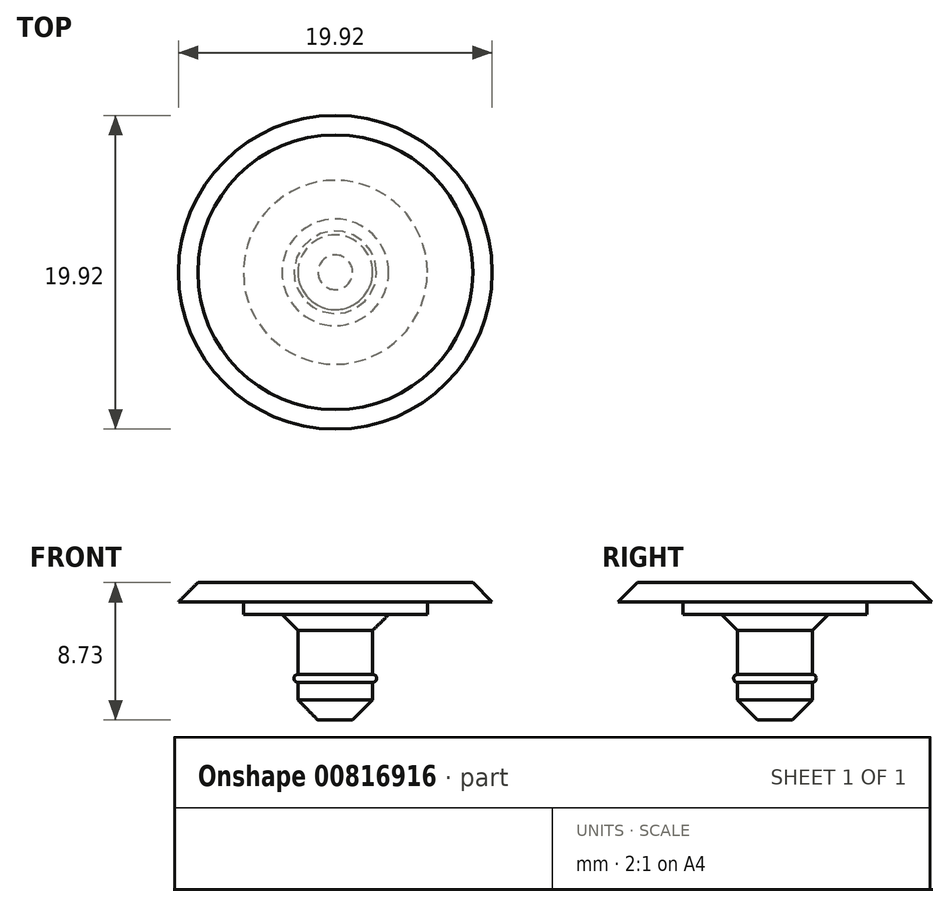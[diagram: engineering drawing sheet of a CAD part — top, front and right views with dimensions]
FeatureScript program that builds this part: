
annotation { "Feature Type Name" : "Feature", "Feature Type Description" : "" }
export const myFeature = defineFeature(function(context is Context, id is Id, definition is map)
    precondition{}
    {
        {
            var Q0;
            Q0=qCreatedBy(makeId("Front.planeOp"),FACE);
            var sketch = newSketch(context, id + "F0", { "sketchPlane" : qUnion([Q0])});
            skLineSegment(sketch, "E0", {"start": v(4.22, 0) * mm, "end": v(10, 0) * mm});
            skLineSegment(sketch, "E1", {"start": v(10, 0) * mm, "end": v(10, 2.03) * mm});
            skLineSegment(sketch, "E2", {"start": v(0, 2.03) * mm, "end": v(0, 0) * mm});
            skLineSegment(sketch, "E3", {"start": v(2.37, 0) * mm, "end": v(2.68, 0) * mm});
            skLineSegment(sketch, "E4", {"start": v(2.37, 0) * mm, "end": v(2.37, -3.8) * mm});
            skLineSegment(sketch, "E5", {"start": v(2.37, -6.7) * mm, "end": v(0, -6.7) * mm});
            skLineSegment(sketch, "E6", {"start": v(0, -6.7) * mm, "end": v(0, 0) * mm});
            skArc(sketch, "E7", {"start": v(2.37, -4.3) * mm, "mid": v(2.63, -4.05) * mm, "end": v(2.37, -3.8) * mm});
            skLineSegment(sketch, "E8.trimOffspring", {"start": v(2.37, -4.3) * mm, "end": v(2.37, -6.7) * mm});
            skLineSegment(sketch, "E9", {"start": v(2.68, 0) * mm, "end": v(4.22, 0) * mm});
            skLineSegment(sketch, "E10", {"start": v(0, 2.03) * mm, "end": v(10, 2.03) * mm});
            skPoint(sketch, "E11.center.orphan", {"position": v(0, 15.24) * mm});
            skSolve(sketch);
        }
        {
            var Q0;
            Q0=qSketchRegion(id+"F0",true);
            var Q1;
            Q1=sQuery(id+"F0.wireOp",EDGE,"E2");
            revolve(context, id + "F1", {"surfaceOperationType" : NewSurfaceOperationType.NEW, "entities" : qUnion([Q0]), "axis" : qUnion([Q1]), "revolveType" : RevolveType.FULL});
        }
        {
            var Q0;
            Q0=makeQuery(id+"F1.opRevolve","SWEPT_EDGE",EDGE,{"disambiguationData":[OSD([sQuery(id+"F0.wireOp",EDGE,"E5"),sQuery(id+"F0.wireOp",EDGE,"E8.trimOffspring")])]});
            chamfer(context, id + "F2", {"entities" : qUnion([Q0]), "width" : 1.27 * mm, "tangentPropagation" : true});
        }
        {
            var Q0;
            Q0=makeQuery(id+"F1.opRevolve","SWEPT_FACE",FACE,{"disambiguationData":[OSD([sQuery(id+"F0.wireOp",EDGE,"E0"),sQuery(id+"F0.wireOp",EDGE,"E3"),sQuery(id+"F0.wireOp",EDGE,"E9")])]});
            var sketch = newSketch(context, id + "F3", { "sketchPlane" : qUnion([Q0])});
            skCircle(sketch, "E12", {"center": v(0, 0) * mm, "radius": 5.84 * mm});
            skCircle(sketch, "E13", {"center": v(0, 0) * mm, "radius": 14.28 * mm});
            skSolve(sketch);
        }
        {
            var Q0;
            Q0=makeQuery(id+"F3.imprint","IMPRINT",FACE,{"disambiguationData":[TD([[makeQuery(id+"F3.imprint","IMPRINT",EDGE,{"derivedFrom":sQuery(id+"F3.wireOp",EDGE,"E13")}),1.0]])]});
            var Q1;
            Q1=makeQuery(id+"F3.imprint","IMPRINT",FACE,{"disambiguationData":[TD([[makeQuery(id+"F3.imprint","IMPRINT",EDGE,{"derivedFrom":sQuery(id+"F3.wireOp",EDGE,"E12")}),-1.0]])]});
            extrude(context, id + "F4", {"entities" : qUnion([Q0, Q1]), "operationType" : NewBodyOperationType.REMOVE, "oppositeDirection" : true, "depth" : .8 * mm, "offsetDistance" : 25.4 * mm});
        }
        {
            var Q0;
            Q0=makeQuery(id+"F1.opRevolve","SWEPT_EDGE",EDGE,{"disambiguationData":[OSD([sQuery(id+"F0.wireOp",EDGE,"E3"),sQuery(id+"F0.wireOp",EDGE,"E4")])]});
            chamfer(context, id + "F5", {"entities" : qUnion([Q0]), "width" : 1.02 * mm, "tangentPropagation" : true});
        }
        {
            var Q0;
            Q0=makeQuery(id+"F1.opRevolve","SWEPT_EDGE",EDGE,{"disambiguationData":[OSD([sQuery(id+"F0.wireOp",EDGE,"E1"),sQuery(id+"F0.wireOp",EDGE,"E10")])]});
            chamfer(context, id + "F6", {"entities" : qUnion([Q0]), "width" : 1.27 * mm, "tangentPropagation" : true});
        }
    });
